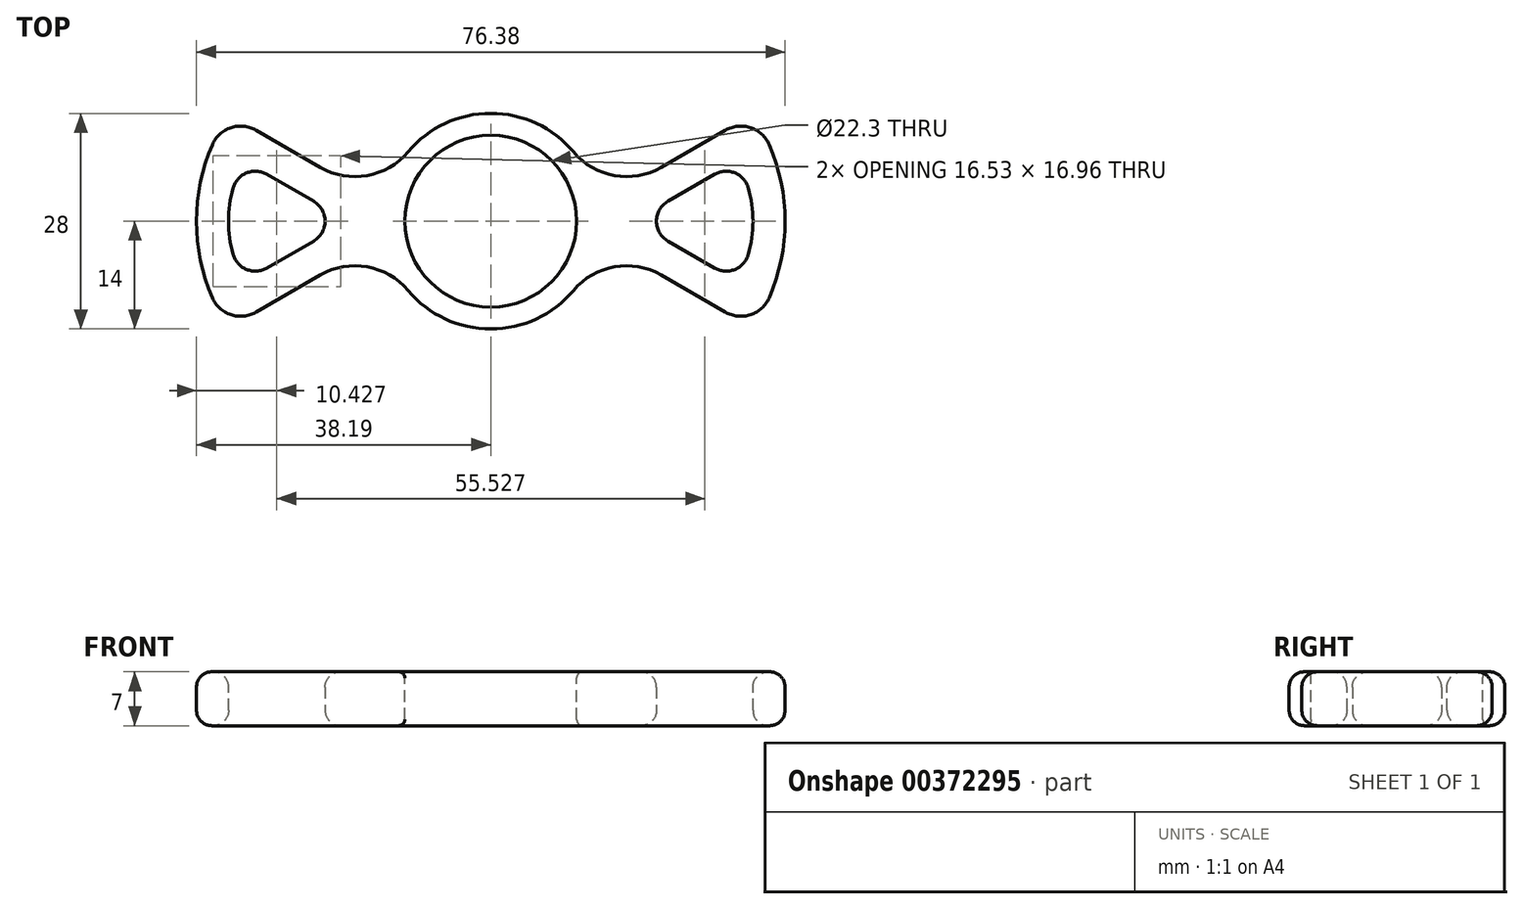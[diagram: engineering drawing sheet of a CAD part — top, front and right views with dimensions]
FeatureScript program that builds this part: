
annotation { "Feature Type Name" : "Feature", "Feature Type Description" : "" }
export const myFeature = defineFeature(function(context is Context, id is Id, definition is map)
    precondition{}
    {
        {
            var Q0;
            Q0=qCreatedBy(makeId("Top.planeOp"),FACE);
            var sketch = newSketch(context, id + "F0", { "sketchPlane" : qUnion([Q0])});
            skArc(sketch, "E0", {"start": v(-13.82, -2.2) * mm, "mid": v(0, -14) * mm, "end": v(13.82, -2.2) * mm});
            skCircle(sketch, "E1.cCircle", {"center": v(-26, 0) * mm, "radius": 16 * mm, "construction": true});
            skLineSegment(sketch, "E1.0", {"start": v(-13.82, -2.2) * mm, "end": v(-34, -13.86) * mm});
            skLineSegment(sketch, "E1.2", {"start": v(-34, 13.86) * mm, "end": v(-13.82, 2.2) * mm});
            skCircle(sketch, "E2.cCircle", {"center": v(26, 0) * mm, "radius": 16 * mm, "construction": true});
            skLineSegment(sketch, "E2.0", {"start": v(13.82, 2.2) * mm, "end": v(34, 13.86) * mm});
            skLineSegment(sketch, "E2.2", {"start": v(34, -13.86) * mm, "end": v(13.82, -2.2) * mm});
            skPoint(sketch, "E3.orphan", {"position": v(-10, 0) * mm});
            skPoint(sketch, "E4.orphan", {"position": v(10, 0) * mm});
            skArc(sketch, "E5.trimOffspring", {"start": v(13.82, 2.2) * mm, "mid": v(0, 14) * mm, "end": v(-13.82, 2.2) * mm});
            skArc(sketch, "E6", {"start": v(-34, 13.86) * mm, "mid": v(-38.2, 0) * mm, "end": v(-34, -13.86) * mm});
            skArc(sketch, "E7", {"start": v(34, -13.86) * mm, "mid": v(38.2, 0) * mm, "end": v(34, 13.86) * mm});
            skSolve(sketch);
        }
        {
            var Q0;
            Q0 = qSketchRegion(id + "F0", true);
            extrude(context, id + "F1", {"entities" : qUnion([Q0]), "depth" : 7 * mm});
        }
        {
            var Q0;
            Q0=makeQuery(id+"F1.opExtrude","CAP_FACE",FACE,{"disambiguationData":[OSD([sQuery(id+"F0.wireOp",EDGE,"E0"),sQuery(id+"F0.wireOp",EDGE,"E1.0"),sQuery(id+"F0.wireOp",EDGE,"E1.1"),sQuery(id+"F0.wireOp",EDGE,"E1.2"),sQuery(id+"F0.wireOp",EDGE,"E2.0"),sQuery(id+"F0.wireOp",EDGE,"E2.1"),sQuery(id+"F0.wireOp",EDGE,"E2.2"),sQuery(id+"F0.wireOp",EDGE,"E5.trimOffspring")])],"isStart":false});
            var sketch = newSketch(context, id + "F2", { "sketchPlane" : qUnion([Q0])});
            skCircle(sketch, "E8", {"center": v(0, 0) * mm, "radius": 11.15 * mm});
            skSolve(sketch);
        }
        {
            var Q0;
            Q0 = qSketchRegion(id + "F2", true);
            extrude(context, id + "F3", {"entities" : qUnion([Q0]), "operationType" : NewBodyOperationType.REMOVE, "endBound" : BoundingType.THROUGH_ALL, "oppositeDirection" : true, "depth" : 25 * mm});
        }
        {
            var Q0;
            Q0=makeQuery(id+"F1.opExtrude","SWEPT_EDGE",EDGE,{"disambiguationData":[OSD([sQuery(id+"F0.wireOp",EDGE,"E0"),sQuery(id+"F0.wireOp",EDGE,"E1.0")])]});
            var Q1;
            Q1=makeQuery(id+"F1.opExtrude","SWEPT_EDGE",EDGE,{"disambiguationData":[OSD([sQuery(id+"F0.wireOp",EDGE,"E0"),sQuery(id+"F0.wireOp",EDGE,"E2.2")])]});
            var Q2;
            Q2=makeQuery(id+"F1.opExtrude","SWEPT_EDGE",EDGE,{"disambiguationData":[OSD([sQuery(id+"F0.wireOp",EDGE,"E2.0"),sQuery(id+"F0.wireOp",EDGE,"E5.trimOffspring")])]});
            var Q3;
            Q3=makeQuery(id+"F1.opExtrude","SWEPT_EDGE",EDGE,{"disambiguationData":[OSD([sQuery(id+"F0.wireOp",EDGE,"E1.2"),sQuery(id+"F0.wireOp",EDGE,"E5.trimOffspring")])]});
            fillet(context, id + "F4", {"entities" : qUnion([Q0, Q1, Q2, Q3]), "radius" : 9 * mm, "tangentPropagation" : true, "allowEdgeOverflow" : false});
        }
        {
            var Q0;
            Q0=makeQuery(id+"F1.opExtrude","SWEPT_EDGE",EDGE,{"disambiguationData":[OSD([sQuery(id+"F0.wireOp",EDGE,"E2.0"),sQuery(id+"F0.wireOp",EDGE,"E2.1")])]});
            var Q1;
            Q1=makeQuery(id+"F1.opExtrude","SWEPT_EDGE",EDGE,{"disambiguationData":[OSD([sQuery(id+"F0.wireOp",EDGE,"E2.1"),sQuery(id+"F0.wireOp",EDGE,"E2.2")])]});
            var Q2;
            Q2=makeQuery(id+"F1.opExtrude","SWEPT_EDGE",EDGE,{"disambiguationData":[OSD([sQuery(id+"F0.wireOp",EDGE,"E1.1"),sQuery(id+"F0.wireOp",EDGE,"E1.2")])]});
            var Q3;
            Q3=makeQuery(id+"F1.opExtrude","SWEPT_EDGE",EDGE,{"disambiguationData":[OSD([sQuery(id+"F0.wireOp",EDGE,"E1.0"),sQuery(id+"F0.wireOp",EDGE,"E1.1")])]});
            fillet(context, id + "F5", {"entities" : qUnion([Q0, Q1, Q2, Q3]), "radius" : 4 * mm, "tangentPropagation" : true, "allowEdgeOverflow" : false});
        }
        {
            var Q0;
            Q0=makeQuery(id+"F1.opExtrude","CAP_FACE",FACE,{"disambiguationData":[OSD([sQuery(id+"F0.wireOp",EDGE,"E0"),sQuery(id+"F0.wireOp",EDGE,"E1.0"),sQuery(id+"F0.wireOp",EDGE,"E1.1"),sQuery(id+"F0.wireOp",EDGE,"E1.2"),sQuery(id+"F0.wireOp",EDGE,"E2.0"),sQuery(id+"F0.wireOp",EDGE,"E2.1"),sQuery(id+"F0.wireOp",EDGE,"E2.2"),sQuery(id+"F0.wireOp",EDGE,"E5.trimOffspring")])],"isStart":false});
            var sketch = newSketch(context, id + "F6", { "sketchPlane" : qUnion([Q0])});
            skCircle(sketch, "E9.cCircle", {"center": v(-27.5, 0) * mm, "radius": 9 * mm, "construction": true});
            skLineSegment(sketch, "E9.0", {"start": v(-18.5, 0) * mm, "end": v(-32, -7.8) * mm});
            skLineSegment(sketch, "E9.2", {"start": v(-32, 7.8) * mm, "end": v(-18.5, 0) * mm});
            skCircle(sketch, "E10.cCircle", {"center": v(27.5, 0) * mm, "radius": 9 * mm, "construction": true});
            skLineSegment(sketch, "E10.0", {"start": v(18.5, 0) * mm, "end": v(32, 7.8) * mm});
            skLineSegment(sketch, "E10.2", {"start": v(32, -7.8) * mm, "end": v(18.5, 0) * mm});
            skArc(sketch, "E11", {"start": v(-32, 7.8) * mm, "mid": v(-34.03, 0) * mm, "end": v(-32, -7.8) * mm});
            skArc(sketch, "E12", {"start": v(32, -7.8) * mm, "mid": v(34.03, 0) * mm, "end": v(32, 7.8) * mm});
            skSolve(sketch);
        }
        {
            var Q0;
            Q0 = qSketchRegion(id + "F6", true);
            extrude(context, id + "F7", {"entities" : qUnion([Q0]), "operationType" : NewBodyOperationType.REMOVE, "endBound" : BoundingType.THROUGH_ALL, "oppositeDirection" : true, "depth" : 25 * mm});
        }
        {
            var Q0;
            Q0=makeQuery(id+"F7.boolean.opBoolean","COPY",EDGE,{"derivedFrom":makeQuery(id+"F7.opExtrude","SWEPT_EDGE",EDGE,{"disambiguationData":[OSD([sQuery(id+"F6.wireOp",EDGE,"E9.1"),sQuery(id+"F6.wireOp",EDGE,"E9.2")])]})});
            var Q1;
            Q1=makeQuery(id+"F7.boolean.opBoolean","COPY",EDGE,{"derivedFrom":makeQuery(id+"F7.opExtrude","SWEPT_EDGE",EDGE,{"disambiguationData":[OSD([sQuery(id+"F6.wireOp",EDGE,"E9.0"),sQuery(id+"F6.wireOp",EDGE,"E9.1")])]})});
            var Q2;
            Q2=makeQuery(id+"F7.boolean.opBoolean","COPY",EDGE,{"derivedFrom":makeQuery(id+"F7.opExtrude","SWEPT_EDGE",EDGE,{"disambiguationData":[OSD([sQuery(id+"F6.wireOp",EDGE,"E9.0"),sQuery(id+"F6.wireOp",EDGE,"E9.2")])]})});
            var Q3;
            Q3=makeQuery(id+"F7.boolean.opBoolean","COPY",EDGE,{"derivedFrom":makeQuery(id+"F7.opExtrude","SWEPT_EDGE",EDGE,{"disambiguationData":[OSD([sQuery(id+"F6.wireOp",EDGE,"E10.0"),sQuery(id+"F6.wireOp",EDGE,"E10.2")])]})});
            var Q4;
            Q4=makeQuery(id+"F7.boolean.opBoolean","COPY",EDGE,{"derivedFrom":makeQuery(id+"F7.opExtrude","SWEPT_EDGE",EDGE,{"disambiguationData":[OSD([sQuery(id+"F6.wireOp",EDGE,"E10.0"),sQuery(id+"F6.wireOp",EDGE,"E10.1")])]})});
            var Q5;
            Q5=makeQuery(id+"F7.boolean.opBoolean","COPY",EDGE,{"derivedFrom":makeQuery(id+"F7.opExtrude","SWEPT_EDGE",EDGE,{"disambiguationData":[OSD([sQuery(id+"F6.wireOp",EDGE,"E10.1"),sQuery(id+"F6.wireOp",EDGE,"E10.2")])]})});
            fillet(context, id + "F8", {"entities" : qUnion([Q0, Q1, Q2, Q3, Q4, Q5]), "radius" : 3 * mm, "tangentPropagation" : true, "allowEdgeOverflow" : false});
        }
        {
            var Q0;
            Q0=makeQuery(id+"F3.boolean.opBoolean","COPY",FACE,{"derivedFrom":makeQuery(id+"F3.opExtrude","SWEPT_FACE",FACE,{"disambiguationData":[OSD([sQuery(id+"F2.wireOp",EDGE,"E8")])]})});
            fillet(context, id + "F9", {"entities" : qUnion([Q0]), "radius" : .8 * mm, "tangentPropagation" : true, "allowEdgeOverflow" : false});
        }
        {
            var Q0;
            Q0=makeQuery(id+"F1.opExtrude","CAP_FACE",FACE,{"disambiguationData":[OSD([sQuery(id+"F0.wireOp",EDGE,"E0"),sQuery(id+"F0.wireOp",EDGE,"E1.0"),sQuery(id+"F0.wireOp",EDGE,"E1.1"),sQuery(id+"F0.wireOp",EDGE,"E1.2"),sQuery(id+"F0.wireOp",EDGE,"E2.0"),sQuery(id+"F0.wireOp",EDGE,"E2.1"),sQuery(id+"F0.wireOp",EDGE,"E2.2"),sQuery(id+"F0.wireOp",EDGE,"E5.trimOffspring")])],"isStart":false});
            var Q1;
            Q1=makeQuery(id+"F1.opExtrude","CAP_FACE",FACE,{"disambiguationData":[OSD([sQuery(id+"F0.wireOp",EDGE,"E0"),sQuery(id+"F0.wireOp",EDGE,"E1.0"),sQuery(id+"F0.wireOp",EDGE,"E1.1"),sQuery(id+"F0.wireOp",EDGE,"E1.2"),sQuery(id+"F0.wireOp",EDGE,"E2.0"),sQuery(id+"F0.wireOp",EDGE,"E2.1"),sQuery(id+"F0.wireOp",EDGE,"E2.2"),sQuery(id+"F0.wireOp",EDGE,"E5.trimOffspring")])],"isStart":true});
            fillet(context, id + "F10", {"entities" : qUnion([Q0, Q1]), "radius" : 2 * mm, "tangentPropagation" : true, "allowEdgeOverflow" : false});
        }
    });
